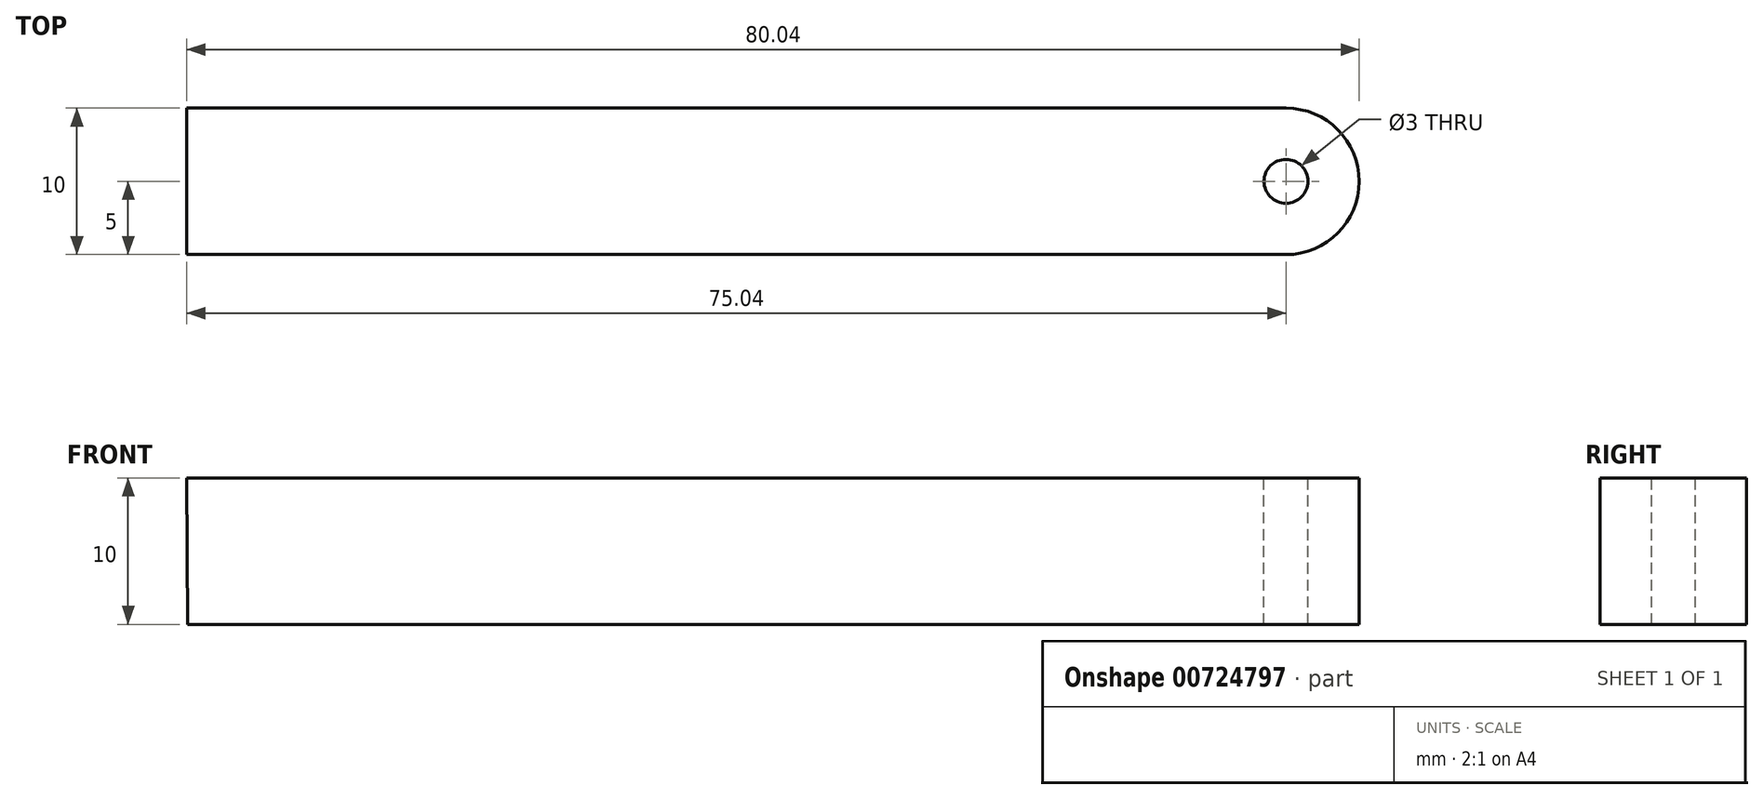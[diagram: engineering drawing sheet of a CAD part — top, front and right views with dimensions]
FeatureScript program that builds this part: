
annotation { "Feature Type Name" : "Feature", "Feature Type Description" : "" }
export const myFeature = defineFeature(function(context is Context, id is Id, definition is map)
    precondition{}
    {
        {
            var Q0;
            Q0=qCreatedBy(makeId("Front.planeOp"),FACE);
            var sketch = newSketch(context, id + "F0", { "sketchPlane" : qUnion([Q0])});
            skLineSegment(sketch, "E0.bottom", {"start": v(44.12, 0) * mm, "end": v(-25.88, 0) * mm});
            skLineSegment(sketch, "E0.top", {"start": v(44.12, 10) * mm, "end": v(-25.92, 10) * mm});
            skLineSegment(sketch, "E0.left", {"start": v(44.12, 0) * mm, "end": v(44.12, 10) * mm});
            skLineSegment(sketch, "E1.bottom", {"start": v(-25.88, 0) * mm, "end": v(-35.88, 0) * mm});
            skLineSegment(sketch, "E2", {"start": v(-25.92, 10) * mm, "end": v(-35.92, 10) * mm});
            skLineSegment(sketch, "E3", {"start": v(-35.92, 10) * mm, "end": v(-35.88, 0) * mm});
            skSolve(sketch);
        }
        {
            var Q0;
            Q0 = qSketchRegion(id + "F0", true);
            extrude(context, id + "F1", {"entities" : qUnion([Q0]), "depth" : 10 * mm, "offsetDistance" : 25 * mm});
        }
        {
            var Q0;
            Q0=makeQuery(id+"F1.opExtrude","SWEPT_FACE",FACE,{"disambiguationData":[OSD([sQuery(id+"F0.wireOp",EDGE,"E0.top")])]});
            var sketch = newSketch(context, id + "F2", { "sketchPlane" : qUnion([Q0])});
            skLineSegment(sketch, "E4", {"start": v(44.12, -5) * mm, "end": v(39.12, -5) * mm, "construction": true});
            skCircle(sketch, "E5", {"center": v(39.12, -5) * mm, "radius": 1.5 * mm});
            skSolve(sketch);
        }
        {
            var Q0;
            Q0=sQuery(id+"F2.wireOp",VERTEX,"E5.center");
            var Q1;
            Q1=makeQuery(id+"F1.opExtrude","SWEPT_BODY",BODY,{"disambiguationData":[OSD([sQuery(id+"F0.wireOp",EDGE,"E0.bottom"),sQuery(id+"F0.wireOp",EDGE,"E0.top"),sQuery(id+"F0.wireOp",EDGE,"E0.left"),sQuery(id+"F0.wireOp",EDGE,"E1.bottom"),sQuery(id+"F0.wireOp",EDGE,"E1.top"),sQuery(id+"F0.wireOp",EDGE,"E1.left"),sQuery(id+"F0.wireOp",EDGE,"E1.right")])]});
            hole(context, id + "F3", {"style" : HoleStyle.SIMPLE, "endStyle" : HoleEndStyle.THROUGH, "holeDiameter" : 3 * mm, "majorDiameter" : 5 * mm, "isTappedThrough" : true, "tappedDepth" : 12 * mm, "tapClearance" : 3, "locations" : qUnion([Q0]), "scope" : qUnion([Q1])});
        }
        {
            var Q0;
            Q0=makeQuery(id+"F1.opExtrude","CAP_EDGE",EDGE,{"disambiguationData":[OSD([sQuery(id+"F0.wireOp",EDGE,"E0.left")])],"isStart":false});
            var Q1;
            Q1=makeQuery(id+"F1.opExtrude","CAP_EDGE",EDGE,{"disambiguationData":[OSD([sQuery(id+"F0.wireOp",EDGE,"E0.left")])],"isStart":true});
            fillet(context, id + "F4", {"entities" : qUnion([Q0, Q1]), "radius" : 5 * mm, "tangentPropagation" : true, "allowEdgeOverflow" : false});
        }
    });
